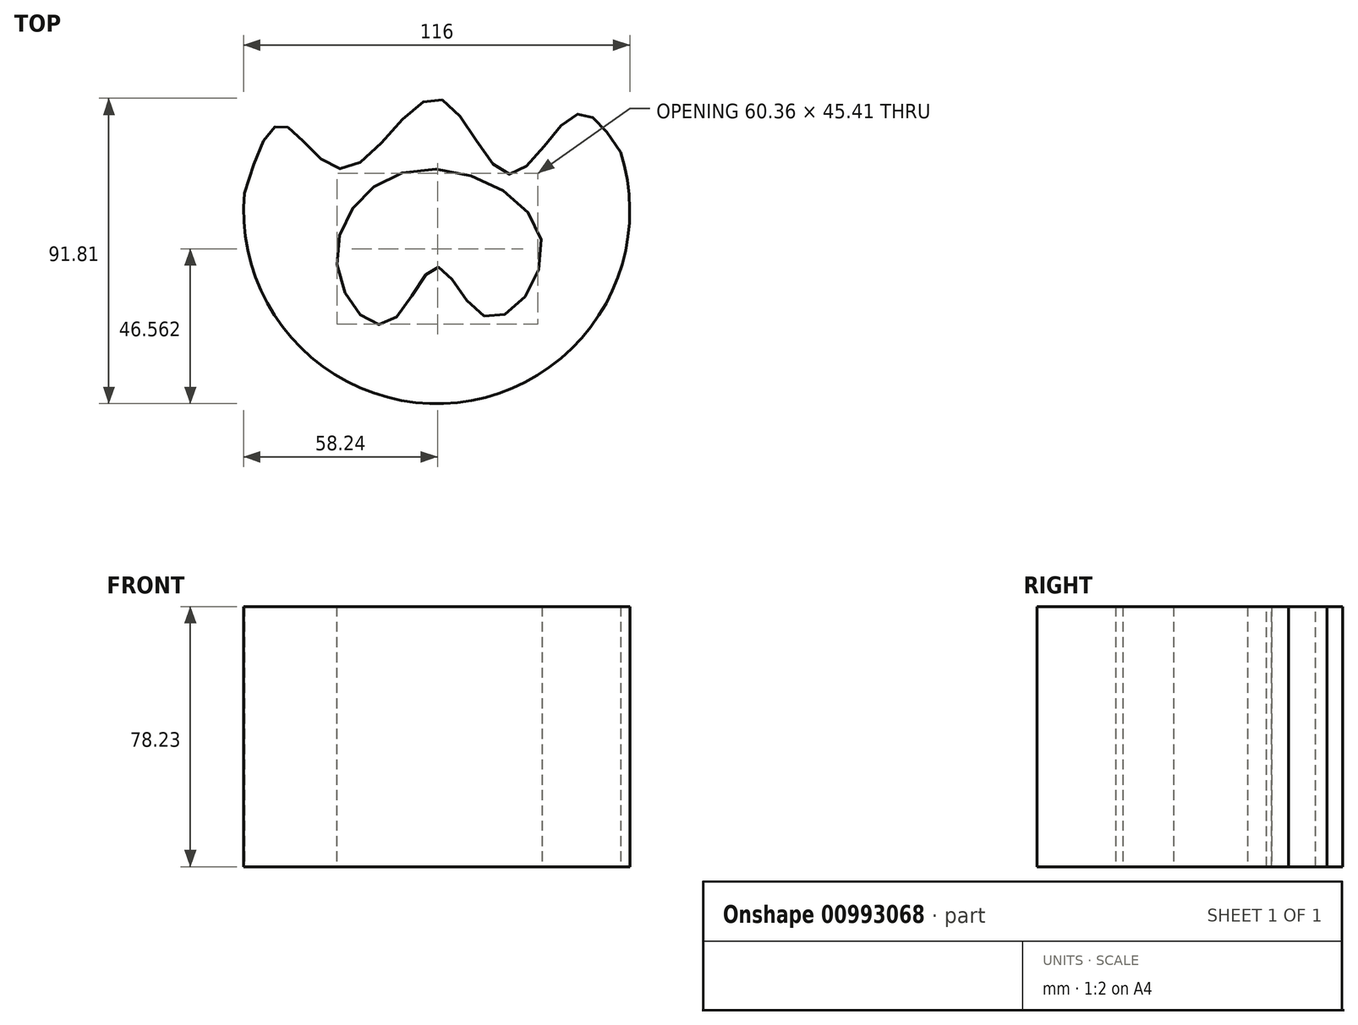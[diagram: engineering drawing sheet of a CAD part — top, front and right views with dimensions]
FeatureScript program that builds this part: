
annotation { "Feature Type Name" : "Feature", "Feature Type Description" : "" }
export const myFeature = defineFeature(function(context is Context, id is Id, definition is map)
    precondition{}
    {
        {
            var Q0;
            Q0=qCreatedBy(makeId("Top.planeOp"),FACE);
            var sketch = newSketch(context, id + "F0", { "sketchPlane" : qUnion([Q0])});
            skArc(sketch, "E0", {"start": v(-57.75, 5.32) * mm, "mid": v(6.29, -57.66) * mm, "end": v(55.25, 17.64) * mm});
            skFitSpline(sketch, "E1", {"points": [v(-57.75, 5.32) * mm, v(-46.14, 25.68) * mm, v(-27.6, 12.55) * mm, v(0, 33.78) * mm, v(21.43, 11) * mm, v(41.5, 28.76) * mm, v(55.25, 17.64) * mm], "startDerivative": vector(62.93, 203.16) * mm, "endDerivative": vector(94.21, -144.76) * mm});
            skSolve(sketch);
        }
        {
            var Q0;
            Q0=makeQuery(id+"F0.imprint","IMPRINT",FACE,{"disambiguationData":[TD([[makeQuery(id+"F0.imprint","IMPRINT",EDGE,{"derivedFrom":sQuery(id+"F0.wireOp",EDGE,"E0")}),1.0]])]});
            extrude(context, id + "F1", {"entities" : qUnion([Q0]), "depth" : 78.23 * mm, "offsetDistance" : 25.4 * mm});
        }
        {
            var Q0;
            Q0=makeQuery(id+"F1.opExtrude","CAP_FACE",FACE,{"disambiguationData":[OSD([sQuery(id+"F0.wireOp",EDGE,"E0"),sQuery(id+"F0.wireOp",EDGE,"E1")])],"isStart":false});
            var sketch = newSketch(context, id + "F2", { "sketchPlane" : qUnion([Q0])});
            skFitSpline(sketch, "E2", {"points": [v(-29.94, -16.14) * mm, v(-7.55, 12.04) * mm, v(31.45, -9.2) * mm, v(15.23, -31.97) * mm, v(0, -16.91) * mm, v(-14.88, -33.9) * mm, v(-29.94, -16.14) * mm]});
            skSolve(sketch);
        }
        {
            var Q0;
            Q0=makeQuery(id+"F2.imprint","IMPRINT",FACE,{"disambiguationData":[TD([[makeQuery(id+"F2.imprint","IMPRINT",EDGE,{"derivedFrom":sQuery(id+"F2.wireOp",EDGE,"E2")}),-1.0]])]});
            extrude(context, id + "F3", {"entities" : qUnion([Q0]), "operationType" : NewBodyOperationType.REMOVE, "oppositeDirection" : true, "depth" : 227.84 * mm, "offsetDistance" : 25.4 * mm});
        }
    });
